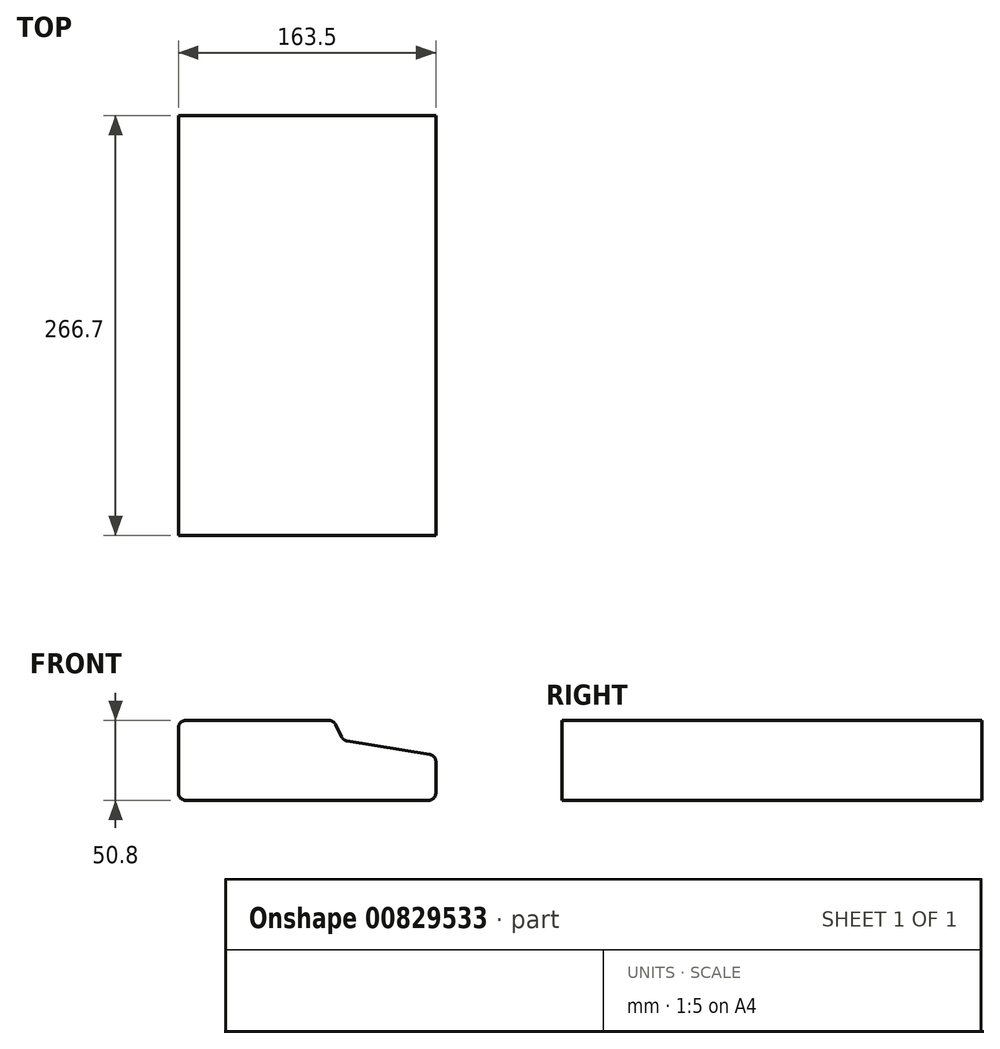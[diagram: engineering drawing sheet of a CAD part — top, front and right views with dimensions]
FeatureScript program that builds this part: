
annotation { "Feature Type Name" : "Feature", "Feature Type Description" : "" }
export const myFeature = defineFeature(function(context is Context, id is Id, definition is map)
    precondition{}
    {
        {
            var Q0;
            Q0=qCreatedBy(makeId("Front.planeOp"),FACE);
            var sketch = newSketch(context, id + "F0", { "sketchPlane" : qUnion([Q0])});
            skLineSegment(sketch, "E0", {"start": v(0, 4.75) * mm, "end": v(0, 46.05) * mm});
            skLineSegment(sketch, "E1", {"start": v(4.75, 50.8) * mm, "end": v(95.49, 50.8) * mm});
            skLineSegment(sketch, "E2", {"start": v(99.74, 48.17) * mm, "end": v(103.69, 40.28) * mm});
            skLineSegment(sketch, "E3", {"start": v(107.18, 37.71) * mm, "end": v(159.51, 29.22) * mm});
            skLineSegment(sketch, "E4", {"start": v(163.5, 24.53) * mm, "end": v(163.5, 4.75) * mm});
            skLineSegment(sketch, "E5", {"start": v(158.75, 0) * mm, "end": v(4.75, 0) * mm});
            skPoint(sketch, "E6.visualSharp", {"position": v(0, 50.8) * mm});
            skArc(sketch, "E6.filletArc", {"start": v(4.75, 50.8) * mm, "mid": v(1.4, 49.4) * mm, "end": v(0, 46.05) * mm});
            skPoint(sketch, "E7.visualSharp", {"position": v(98.43, 50.8) * mm});
            skArc(sketch, "E7.filletArc", {"start": v(99.74, 48.17) * mm, "mid": v(97.99, 50.1) * mm, "end": v(95.49, 50.8) * mm});
            skPoint(sketch, "E8.visualSharp", {"position": v(104.78, 38.1) * mm});
            skArc(sketch, "E8.filletArc", {"start": v(103.69, 40.28) * mm, "mid": v(105.12, 38.57) * mm, "end": v(107.18, 37.71) * mm});
            skPoint(sketch, "E9.visualSharp", {"position": v(163.5, 28.57) * mm});
            skArc(sketch, "E9.filletArc", {"start": v(163.5, 24.53) * mm, "mid": v(162.37, 27.61) * mm, "end": v(159.51, 29.22) * mm});
            skPoint(sketch, "E10.visualSharp", {"position": v(163.5, 0) * mm});
            skArc(sketch, "E10.filletArc", {"start": v(158.75, 0) * mm, "mid": v(162.1, 1.4) * mm, "end": v(163.5, 4.75) * mm});
            skPoint(sketch, "E11.visualSharp", {"position": v(0, 0) * mm});
            skArc(sketch, "E11.filletArc", {"start": v(0, 4.75) * mm, "mid": v(1.4, 1.4) * mm, "end": v(4.75, 0) * mm});
            skSolve(sketch);
        }
        {
            var Q0;
            Q0=makeQuery(id+"F0.imprint","IMPRINT",FACE,{"disambiguationData":[TD([[makeQuery(id+"F0.imprint","IMPRINT",EDGE,{"derivedFrom":sQuery(id+"F0.wireOp",EDGE,"E0")}),-1.0]])]});
            extrude(context, id + "F1", {"entities" : qUnion([Q0]), "depth" : 266.7 * mm, "offsetDistance" : 25.4 * mm});
        }
    });
